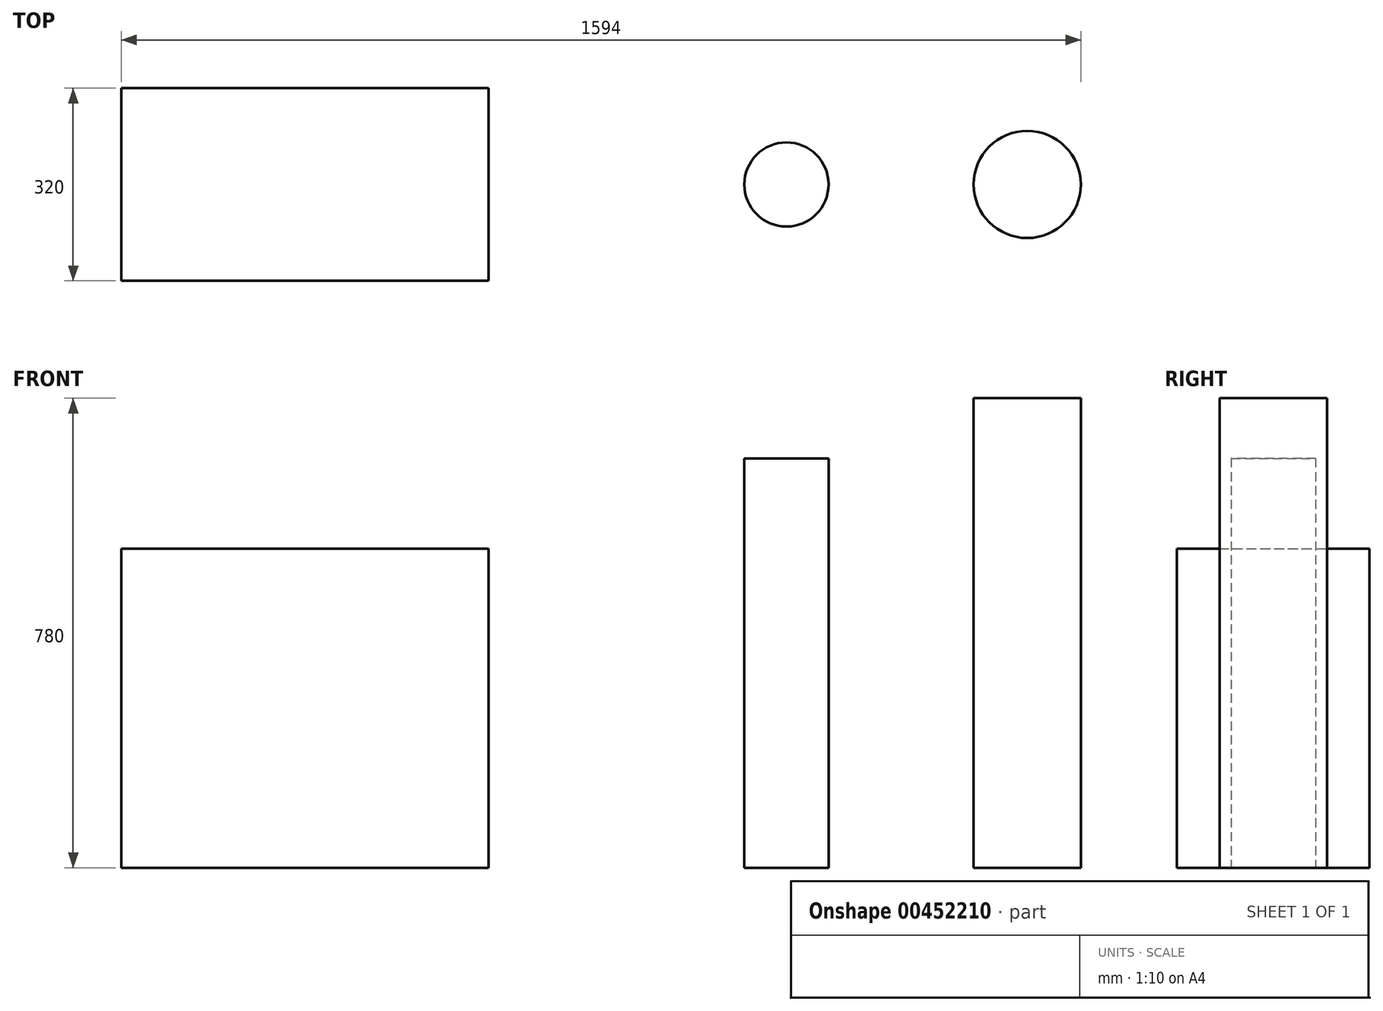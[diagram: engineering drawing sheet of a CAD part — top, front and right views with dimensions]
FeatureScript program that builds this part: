
annotation { "Feature Type Name" : "Feature", "Feature Type Description" : "" }
export const myFeature = defineFeature(function(context is Context, id is Id, definition is map)
    precondition{}
    {
        {
            var Q0;
            Q0=qCreatedBy(makeId("Top.planeOp"),FACE);
            var sketch = newSketch(context, id + "F0", { "sketchPlane" : qUnion([Q0])});
            skLineSegment(sketch, "E0.bottom", {"start": v(305, -160) * mm, "end": v(-305, -160) * mm});
            skLineSegment(sketch, "E0.top", {"start": v(305, 160) * mm, "end": v(-305, 160) * mm});
            skLineSegment(sketch, "E0.left", {"start": v(305, -160) * mm, "end": v(305, 160) * mm});
            skLineSegment(sketch, "E0.right", {"start": v(-305, -160) * mm, "end": v(-305, 160) * mm});
            skPoint(sketch, "E0.middle", {"position": v(0, 0) * mm});
            skSolve(sketch);
        }
        {
            var Q0;
            Q0=qSketchRegion(id+"F0",true);
            extrude(context, id + "F1", {"entities" : qUnion([Q0]), "depth" : 530 * mm});
        }
        {
            var Q0;
            Q0=qCreatedBy(makeId("Top.planeOp"),FACE);
            var sketch = newSketch(context, id + "F2", { "sketchPlane" : qUnion([Q0])});
            skCircle(sketch, "E1", {"center": v(800, 0) * mm, "radius": 70 * mm});
            skCircle(sketch, "E2", {"center": v(1200, 0) * mm, "radius": 89 * mm});
            skSolve(sketch);
        }
        {
            var Q0;
            Q0=makeQuery(id+"F2.imprint","IMPRINT",FACE,{"disambiguationData":[TD([[makeQuery(id+"F2.imprint","IMPRINT",EDGE,{"derivedFrom":sQuery(id+"F2.wireOp",EDGE,"E1")}),1.0]])]});
            extrude(context, id + "F3", {"entities" : qUnion([Q0]), "depth" : 680 * mm});
        }
        {
            var Q0;
            Q0=makeQuery(id+"F2.imprint","IMPRINT",FACE,{"disambiguationData":[TD([[makeQuery(id+"F2.imprint","IMPRINT",EDGE,{"derivedFrom":sQuery(id+"F2.wireOp",EDGE,"E2")}),1.0]])]});
            extrude(context, id + "F4", {"entities" : qUnion([Q0]), "depth" : 780 * mm});
        }
    });
